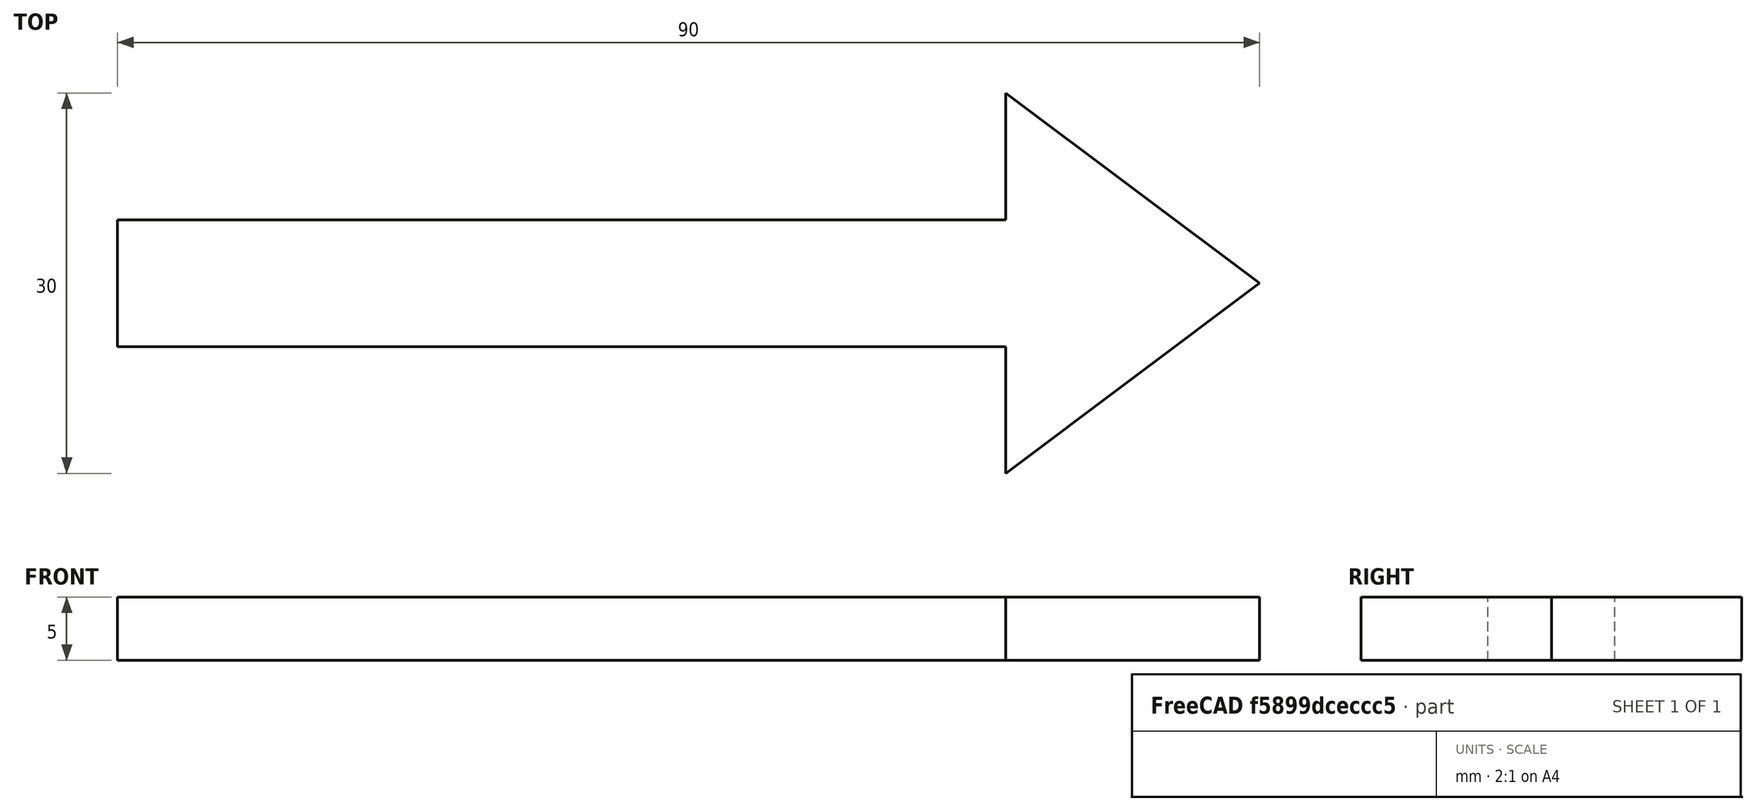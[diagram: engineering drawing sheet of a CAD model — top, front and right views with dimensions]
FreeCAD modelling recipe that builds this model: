
FCSTD DOCUMENT  (FreeCAD 0.16R6707 (Git))
Label: Flecha
License: CreativeCommons Attribution-ShareAlike
LicenseURL: http://creativecommons.org/licenses/by-sa/4.0/
objects: Sketcher::SketchObject×1, PartDesign::Pad×1
note: 3 computed .brp shape members not serialized (recipe doc carries the construction recipe); baked Part::Feature solids carry a one-line shape summary decoded from their .brp

FEATURE [Sketcher::SketchObject] Sketch  label="Boceto_flecha"
  sketch-geometry (7):
    g0: LineSegment StartX=0 StartY=0 StartZ=0 EndX=0 EndY=10 EndZ=0
    g1: LineSegment StartX=0 StartY=10 StartZ=0 EndX=20 EndY=-4.97679 EndZ=0
    g2: LineSegment StartX=20 StartY=-4.97679 StartZ=0 EndX=0 EndY=-20 EndZ=0
    g3: LineSegment StartX=0 StartY=-20 StartZ=0 EndX=0 EndY=-10 EndZ=0
    g4: LineSegment StartX=0 StartY=-10 StartZ=0 EndX=-70 EndY=-10 EndZ=0
    g5: LineSegment StartX=-70 StartY=-10 StartZ=0 EndX=-70 EndY=0 EndZ=0
    g6: LineSegment StartX=-70 StartY=0 StartZ=0 EndX=0 EndY=0 EndZ=0
  constraints (6):
    c: Coincident(g0,g1)
    c: Coincident(g1,g2)
    c: Coincident(g2,g3)
    c: Coincident(g3,g4)
    c: Coincident(g4,g5)
    c: Coincident(g5,g6)
FEATURE [PartDesign::Pad] Pad  label="Flecha"
  Length = 5
  Length2 = 100
  Sketch = -> Sketch
  Type = 0
